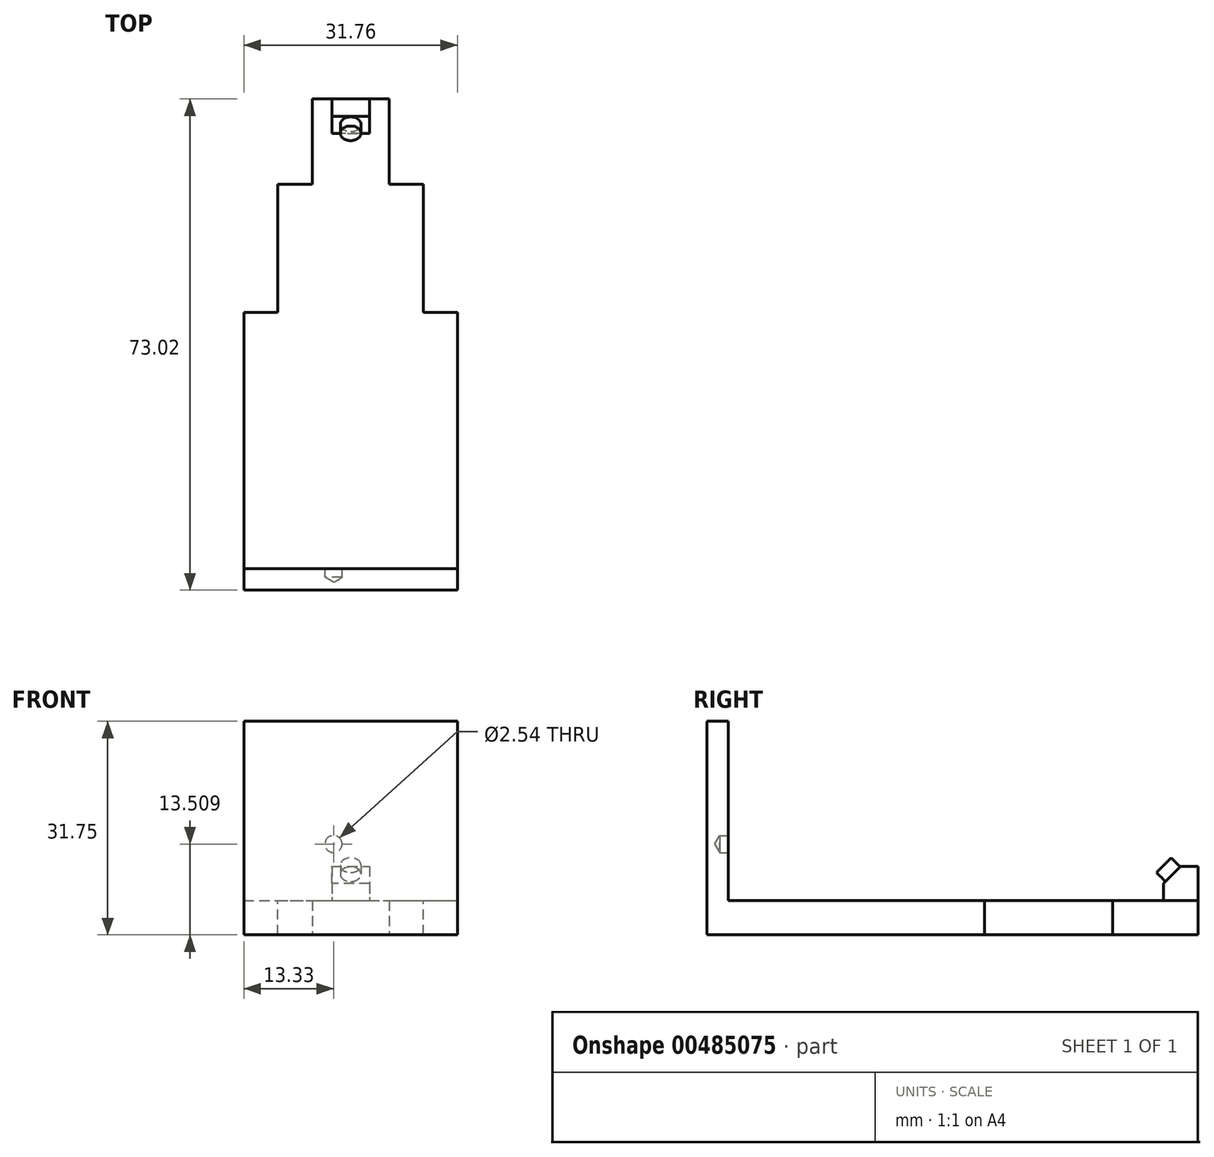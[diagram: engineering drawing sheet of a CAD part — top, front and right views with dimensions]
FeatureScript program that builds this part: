
annotation { "Feature Type Name" : "Feature", "Feature Type Description" : "" }
export const myFeature = defineFeature(function(context is Context, id is Id, definition is map)
    precondition{}
    {
        {
            var Q0;
            Q0=qCreatedBy(makeId("Top.planeOp"),FACE);
            var sketch = newSketch(context, id + "F0", { "sketchPlane" : qUnion([Q0])});
            skLineSegment(sketch, "E0.bottom", {"start": v(-15.88, 15.88) * mm, "end": v(15.88, 15.88) * mm});
            skLineSegment(sketch, "E0.top", {"start": v(-15.88, -15.88) * mm, "end": v(15.88, -15.88) * mm});
            skLineSegment(sketch, "E0.left", {"start": v(-15.87, 15.88) * mm, "end": v(-15.88, -15.88) * mm});
            skLineSegment(sketch, "E0.right", {"start": v(15.88, 15.88) * mm, "end": v(15.88, -15.88) * mm});
            skPoint(sketch, "E0.middle", {"position": v(0, 0) * mm});
            skSolve(sketch);
        }
        {
            var Q0;
            Q0 = qSketchRegion(id + "F0", true);
            extrude(context, id + "F1", {"entities" : qUnion([Q0]), "depth" : 3.17 * mm});
        }
        {
            var Q0;
            Q0=makeQuery(id+"F1.opExtrude","CAP_FACE",FACE,{"disambiguationData":[OSD([sQuery(id+"F0.wireOp",EDGE,"E0.bottom"),sQuery(id+"F0.wireOp",EDGE,"E0.top"),sQuery(id+"F0.wireOp",EDGE,"E0.left"),sQuery(id+"F0.wireOp",EDGE,"E0.right")])],"isStart":false});
            var sketch = newSketch(context, id + "F2", { "sketchPlane" : qUnion([Q0])});
            skPoint(sketch, "E1", {"position": v(-2.55, 2.37) * mm});
            skSolve(sketch);
        }
        {
            var Q0;
            Q0=sQuery(id+"F2.wireOp",VERTEX,"E1");
            var Q1;
            Q1=makeQuery(id+"F1.opExtrude","SWEPT_BODY",BODY,{"disambiguationData":[OSD([sQuery(id+"F0.wireOp",EDGE,"E0.bottom"),sQuery(id+"F0.wireOp",EDGE,"E0.top"),sQuery(id+"F0.wireOp",EDGE,"E0.left"),sQuery(id+"F0.wireOp",EDGE,"E0.right")])]});
            hole(context, id + "F3", {"style" : HoleStyle.SIMPLE, "endStyle" : HoleEndStyle.BLIND, "holeDiameter" : 2.54 * mm, "holeDepth" : 1.27 * mm, "isTappedThrough" : true, "tappedDepth" : 12.7 * mm, "tapClearance" : 3, "locations" : qUnion([Q0]), "scope" : qUnion([Q1])});
        }
        {
            var Q0;
            Q0=makeQuery(id+"F1.opExtrude","CAP_FACE",FACE,{"disambiguationData":[OSD([sQuery(id+"F0.wireOp",EDGE,"E0.bottom"),sQuery(id+"F0.wireOp",EDGE,"E0.top"),sQuery(id+"F0.wireOp",EDGE,"E0.left"),sQuery(id+"F0.wireOp",EDGE,"E0.right")])],"isStart":false});
            var sketch = newSketch(context, id + "F4", { "sketchPlane" : qUnion([Q0])});
            skLineSegment(sketch, "E2.bottom", {"start": v(-15.88, 15.88) * mm, "end": v(15.88, 15.88) * mm});
            skLineSegment(sketch, "E2.top", {"start": v(-15.88, 10.77) * mm, "end": v(15.88, 10.77) * mm});
            skLineSegment(sketch, "E2.left", {"start": v(-15.88, 15.88) * mm, "end": v(-15.88, 10.77) * mm});
            skLineSegment(sketch, "E2.right", {"start": v(15.88, 15.88) * mm, "end": v(15.88, 10.77) * mm});
            skSolve(sketch);
        }
        {
            var Q0;
            Q0 = qSketchRegion(id + "F4", true);
            extrude(context, id + "F5", {"entities" : qUnion([Q0]), "operationType" : NewBodyOperationType.ADD, "depth" : 38.1 * mm});
        }
        {
            var Q0;
            Q0=makeQuery(id+"F5.opExtrude","CAP_FACE",FACE,{"disambiguationData":[OSD([sQuery(id+"F4.wireOp",EDGE,"E2.bottom"),sQuery(id+"F4.wireOp",EDGE,"E2.top"),sQuery(id+"F4.wireOp",EDGE,"E2.left"),sQuery(id+"F4.wireOp",EDGE,"E2.right")])],"isStart":false});
            var sketch = newSketch(context, id + "F6", { "sketchPlane" : qUnion([Q0])});
            skLineSegment(sketch, "E3.bottom", {"start": v(-10.83, 15.88) * mm, "end": v(10.83, 15.88) * mm});
            skLineSegment(sketch, "E3.top", {"start": v(-10.83, 10.77) * mm, "end": v(10.83, 10.77) * mm});
            skLineSegment(sketch, "E3.left", {"start": v(-10.83, 15.88) * mm, "end": v(-10.83, 10.77) * mm});
            skLineSegment(sketch, "E3.right", {"start": v(10.83, 15.88) * mm, "end": v(10.83, 10.77) * mm});
            skPoint(sketch, "E3.middle", {"position": v(0, 13.32) * mm});
            skPoint(sketch, "E3.middle.positionSnap0", {"position": v(15.88, 13.32) * mm});
            skPoint(sketch, "E3.middle.positionSnap1", {"position": v(0, 10.77) * mm});
            skPoint(sketch, "E3.centerSnap0", {"position": v(15.88, 13.32) * mm});
            skPoint(sketch, "E3.centerSnap1", {"position": v(0, 10.77) * mm});
            skSolve(sketch);
        }
        {
            var Q0;
            Q0 = qSketchRegion(id + "F6", true);
            extrude(context, id + "F7", {"entities" : qUnion([Q0]), "operationType" : NewBodyOperationType.ADD, "depth" : 19.05 * mm});
        }
        {
            var Q0;
            Q0=makeQuery(id+"F7.opExtrude","CAP_FACE",FACE,{"disambiguationData":[OSD([sQuery(id+"F6.wireOp",EDGE,"E3.bottom"),sQuery(id+"F6.wireOp",EDGE,"E3.top"),sQuery(id+"F6.wireOp",EDGE,"E3.left"),sQuery(id+"F6.wireOp",EDGE,"E3.right")])],"isStart":false});
            var sketch = newSketch(context, id + "F8", { "sketchPlane" : qUnion([Q0])});
            skLineSegment(sketch, "E4.bottom", {"start": v(5.7, 10.77) * mm, "end": v(-5.7, 10.77) * mm});
            skLineSegment(sketch, "E4.top", {"start": v(5.7, 15.88) * mm, "end": v(-5.7, 15.88) * mm});
            skLineSegment(sketch, "E4.left", {"start": v(5.7, 10.77) * mm, "end": v(5.7, 15.88) * mm});
            skLineSegment(sketch, "E4.right", {"start": v(-5.7, 10.77) * mm, "end": v(-5.7, 15.88) * mm});
            skPoint(sketch, "E4.middle", {"position": v(0, 13.32) * mm});
            skPoint(sketch, "E4.middle.positionSnap0", {"position": v(0, 10.77) * mm});
            skPoint(sketch, "E4.middle.positionSnap1", {"position": v(10.83, 13.32) * mm});
            skPoint(sketch, "E4.centerSnap0", {"position": v(0, 10.77) * mm});
            skPoint(sketch, "E4.centerSnap1", {"position": v(10.83, 13.32) * mm});
            skSolve(sketch);
        }
        {
            var Q0;
            Q0 = qSketchRegion(id + "F8", true);
            extrude(context, id + "F9", {"entities" : qUnion([Q0]), "operationType" : NewBodyOperationType.ADD, "depth" : 12.7 * mm});
        }
        {
            var Q0;
            Q0=makeQuery(id+"F9.boolean.opBoolean","MERGE",FACE,{"derivedFrom":[makeQuery(id+"F7.boolean.opBoolean","MERGE",FACE,{"derivedFrom":[makeQuery(id+"F5.opExtrude","SWEPT_FACE",FACE,{"disambiguationData":[OSD([sQuery(id+"F4.wireOp",EDGE,"E2.top")])]}),makeQuery(id+"F7.opExtrude","SWEPT_FACE",FACE,{"disambiguationData":[OSD([sQuery(id+"F6.wireOp",EDGE,"E3.top")])]})]}),makeQuery(id+"F9.opExtrude","SWEPT_FACE",FACE,{"disambiguationData":[OSD([sQuery(id+"F8.wireOp",EDGE,"E4.bottom")])]})]});
            var sketch = newSketch(context, id + "F10", { "sketchPlane" : qUnion([Q0])});
            skLineSegment(sketch, "E5.bottom", {"start": v(-2.8, 73.03) * mm, "end": v(2.8, 73.03) * mm});
            skLineSegment(sketch, "E5.top", {"start": v(-2.8, 67.9) * mm, "end": v(2.8, 67.9) * mm});
            skLineSegment(sketch, "E5.left", {"start": v(-2.8, 73.03) * mm, "end": v(-2.8, 67.9) * mm});
            skLineSegment(sketch, "E5.right", {"start": v(2.8, 73.03) * mm, "end": v(2.8, 67.9) * mm});
            skPoint(sketch, "E5.middle", {"position": v(0, 70.47) * mm});
            skSolve(sketch);
        }
        {
            var Q0;
            Q0 = qSketchRegion(id + "F10", true);
            extrude(context, id + "F11", {"entities" : qUnion([Q0]), "operationType" : NewBodyOperationType.ADD, "depth" : 5.08 * mm});
        }
        {
            var Q0;
            Q0=makeQuery(id+"F11.opExtrude","CAP_EDGE",EDGE,{"disambiguationData":[OSD([sQuery(id+"F10.wireOp",EDGE,"E5.top")])],"isStart":false});
            chamfer(context, id + "F12", {"entities" : qUnion([Q0]), "width" : 2.54 * mm, "tangentPropagation" : true});
        }
        {
            var Q0;
            Q0=qCreatedBy(makeId("Right.planeOp"),FACE);
            var sketch = newSketch(context, id + "F13", { "sketchPlane" : qUnion([Q0])});
            skLineSegment(sketch, "E6", {"start": v(15.88, 0) * mm, "end": v(15.88, 0) * mm});
            skLineSegment(sketch, "E7", {"start": v(15.88, 0) * mm, "end": v(54.44, 0) * mm});
            skCircle(sketch, "E8", {"center": v(15.88, 0) * mm, "radius": 51.95 * mm});
            skSolve(sketch);
        }
        {
            var Q0;
            Q0=makeQuery(id+"F1.opExtrude","SWEPT_BODY",BODY,{"disambiguationData":[OSD([sQuery(id+"F0.wireOp",EDGE,"E0.bottom"),sQuery(id+"F0.wireOp",EDGE,"E0.top"),sQuery(id+"F0.wireOp",EDGE,"E0.left"),sQuery(id+"F0.wireOp",EDGE,"E0.right")])]});
            var Q1;
            Q1=sQuery(id+"F13.wireOp",EDGE,"E8");
            transform(context, id + "F14", {"entities" : qUnion([Q0]), "transformType" : TransformType.ROTATION, "transformAxis" : qUnion([Q1]), "angle" : 90 * degree, "oppositeDirection" : true, "makeCopy" : false});
        }
        {
            var Q0;
            Q0=makeQuery(id+"F12.opChamfer","BLEND_FACE",FACE,{"disambiguationData":[OSD([sQuery(id+"F10.wireOp",EDGE,"E5.top")])]});
            var sketch = newSketch(context, id + "F15", { "sketchPlane" : qUnion([Q0])});
            skCircle(sketch, "E9", {"center": v(0, 66.58) * mm, "radius": 1.54 * mm});
            skSolve(sketch);
        }
        {
            var Q0;
            Q0 = qSketchRegion(id + "F15", true);
            extrude(context, id + "F16", {"entities" : qUnion([Q0]), "operationType" : NewBodyOperationType.ADD, "depth" : 1.9 * mm});
        }
    });
